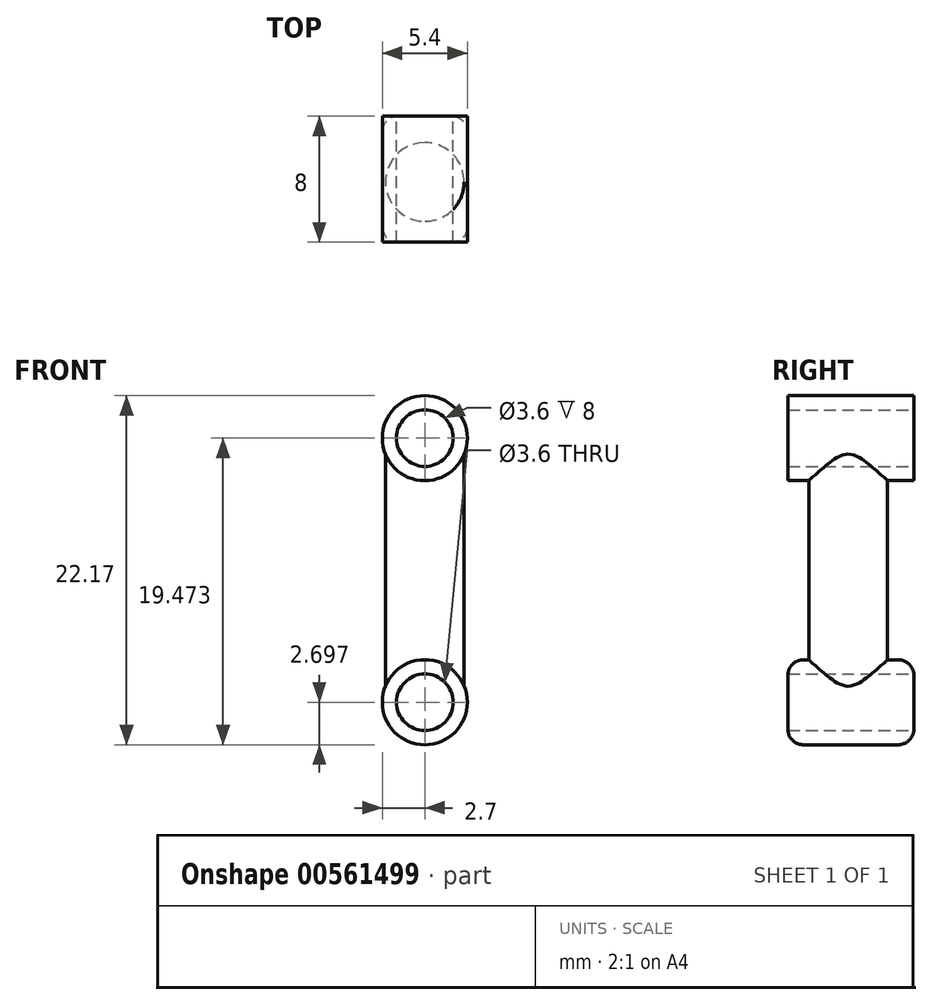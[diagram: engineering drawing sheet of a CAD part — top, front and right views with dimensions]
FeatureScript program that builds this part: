
annotation { "Feature Type Name" : "Feature", "Feature Type Description" : "" }
export const myFeature = defineFeature(function(context is Context, id is Id, definition is map)
    precondition{}
    {
        {
            var Q0;
            Q0=qCreatedBy(makeId("Front.planeOp"),FACE);
            var sketch = newSketch(context, id + "F0", { "sketchPlane" : qUnion([Q0])});
            skCircle(sketch, "E0", {"center": v(0, 0.77) * mm, "radius": 1.8 * mm});
            skCircle(sketch, "E1.0", {"center": v(0, 0.77) * mm, "radius": 2.7 * mm});
            skSolve(sketch);
        }
        {
            var Q0;
            Q0=makeQuery(id+"F0.imprint","IMPRINT",FACE,{"disambiguationData":[TD([[makeQuery(id+"F0.imprint","IMPRINT",EDGE,{"derivedFrom":sQuery(id+"F0.wireOp",EDGE,"E0")}),-1.0]])]});
            extrude(context, id + "F1", {"entities" : qUnion([Q0]), "depth" : 8 * mm, "offsetDistance" : 25 * mm});
        }
        {
            var Q0;
            Q0=qCreatedBy(makeId("Top.planeOp"),FACE);
            var sketch = newSketch(context, id + "F2", { "sketchPlane" : qUnion([Q0])});
            skCircle(sketch, "E2", {"center": v(0, -4.17) * mm, "radius": 2.5 * mm});
            skSolve(sketch);
        }
        {
            var Q0;
            Q0=qSketchRegion(id+"F2",true);
            extrude(context, id + "F3", {"entities" : qUnion([Q0]), "operationType" : NewBodyOperationType.ADD, "oppositeDirection" : true, "depth" : 16 * mm, "offsetDistance" : 25 * mm});
        }
        {
            var Q0;
            Q0=makeQuery(id+"F0.imprint","IMPRINT",FACE,{"disambiguationData":[TD([[makeQuery(id+"F0.imprint","IMPRINT",EDGE,{"derivedFrom":sQuery(id+"F0.wireOp",EDGE,"E0")}),1.0]])]});
            extrude(context, id + "F4", {"entities" : qUnion([Q0]), "operationType" : NewBodyOperationType.REMOVE, "depth" : 25 * mm, "offsetDistance" : 25 * mm});
        }
        {
            var Q0;
            Q0=qCreatedBy(makeId("Front.planeOp"),FACE);
            var sketch = newSketch(context, id + "F5", { "sketchPlane" : qUnion([Q0])});
            skCircle(sketch, "E3", {"center": v(0, -16) * mm, "radius": 1.8 * mm});
            skCircle(sketch, "E4.0", {"center": v(0, -16) * mm, "radius": 2.7 * mm});
            skSolve(sketch);
        }
        {
            var Q0;
            Q0=qSketchRegion(id+"F5",true);
            var Q1;
            Q1=makeQuery(id+"F1.opExtrude","CAP_FACE",FACE,{"disambiguationData":[OSD([sQuery(id+"F0.wireOp",EDGE,"E0"),sQuery(id+"F0.wireOp",EDGE,"E1.0")])],"isStart":false});
            extrude(context, id + "F6", {"entities" : qUnion([Q0]), "operationType" : NewBodyOperationType.ADD, "endBound" : BoundingType.UP_TO_SURFACE, "depth" : 25 * mm, "endBoundEntityFace" : qUnion([Q1]), "offsetDistance" : 25 * mm});
        }
        {
            var Q0;
            Q0=makeQuery(id+"F5.imprint","IMPRINT",FACE,{"disambiguationData":[TD([[makeQuery(id+"F5.imprint","IMPRINT",EDGE,{"derivedFrom":sQuery(id+"F5.wireOp",EDGE,"E3")}),1.0]])]});
            extrude(context, id + "F7", {"entities" : qUnion([Q0]), "operationType" : NewBodyOperationType.REMOVE, "depth" : 25 * mm, "offsetDistance" : 25 * mm});
        }
        {
            var Q0;
            Q0=makeQuery(id+"F6.opExtrude","CAP_EDGE",EDGE,{"disambiguationData":[OSD([sQuery(id+"F5.wireOp",EDGE,"E4.0")])],"isStart":true});
            fillet(context, id + "F8", {"entities" : qUnion([Q0]), "radius" : 1 * mm, "tangentPropagation" : true, "allowEdgeOverflow" : false});
        }
        {
            var Q0;
            Q0=makeQuery(id+"F6.opExtrude","CAP_EDGE",EDGE,{"disambiguationData":[OSD([sQuery(id+"F5.wireOp",EDGE,"E4.0")])],"isStart":false});
            fillet(context, id + "F9", {"entities" : qUnion([Q0]), "radius" : 1 * mm, "tangentPropagation" : true, "allowEdgeOverflow" : false});
        }
    });
